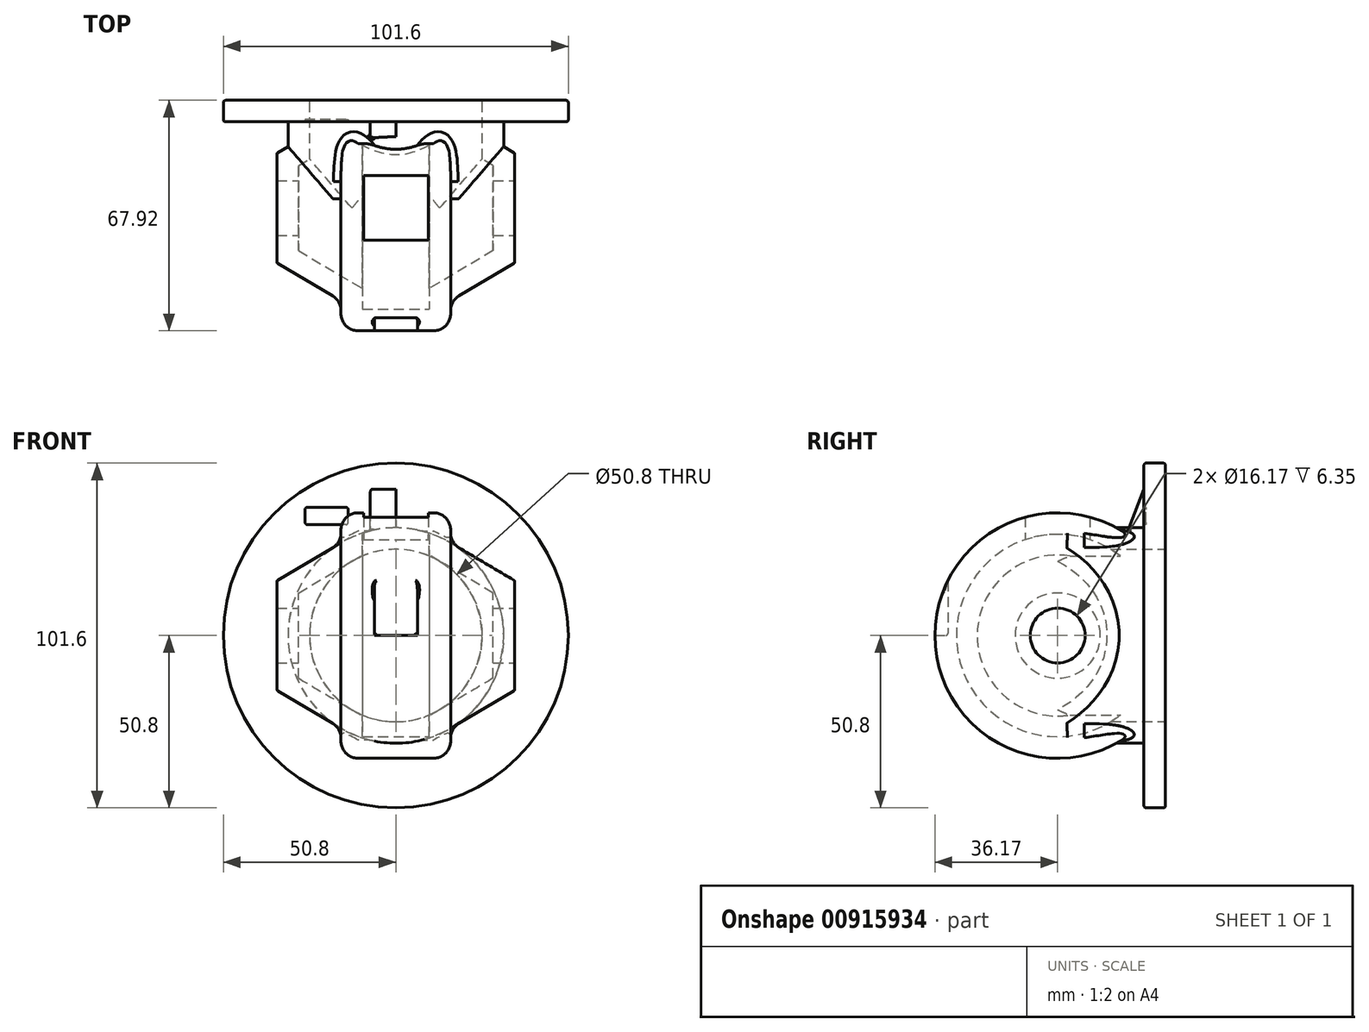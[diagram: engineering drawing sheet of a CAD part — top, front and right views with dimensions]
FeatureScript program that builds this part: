
annotation { "Feature Type Name" : "Feature", "Feature Type Description" : "" }
export const myFeature = defineFeature(function(context is Context, id is Id, definition is map)
    precondition{}
    {
        {
            var Q0;
            Q0=qCreatedBy(makeId("Front.planeOp"),FACE);
            var sketch = newSketch(context, id + "F0", { "sketchPlane" : qUnion([Q0])});
            skCircle(sketch, "E0", {"center": v(0, 0) * mm, "radius": 50.8 * mm});
            skSolve(sketch);
        }
        {
            var Q0;
            Q0=makeQuery(id+"F0.imprint","IMPRINT",FACE,{"disambiguationData":[TD([[makeQuery(id+"F0.imprint","IMPRINT",EDGE,{"derivedFrom":sQuery(id+"F0.wireOp",EDGE,"E0")}),1.0]])]});
            extrude(context, id + "F1", {"entities" : qUnion([Q0]), "depth" : 6.35 * mm, "offsetDistance" : 25.4 * mm});
        }
        {
            var Q0;
            Q0=makeQuery(id+"F1.opExtrude","CAP_FACE",FACE,{"disambiguationData":[OSD([sQuery(id+"F0.wireOp",EDGE,"E0")])],"isStart":false});
            var sketch = newSketch(context, id + "F2", { "sketchPlane" : qUnion([Q0])});
            skCircle(sketch, "E1", {"center": v(0, 0) * mm, "radius": 31.75 * mm});
            skCircle(sketch, "E2", {"center": v(0, 0) * mm, "radius": 25.4 * mm});
            skSolve(sketch);
        }
        {
            var Q0;
            Q0=makeQuery(id+"F2.imprint","IMPRINT",FACE,{"disambiguationData":[TD([[makeQuery(id+"F2.imprint","IMPRINT",EDGE,{"derivedFrom":sQuery(id+"F2.wireOp",EDGE,"E1")}),1.0]])]});
            extrude(context, id + "F3", {"entities" : qUnion([Q0]), "operationType" : NewBodyOperationType.ADD, "depth" : 25.4 * mm, "offsetDistance" : 25.4 * mm});
        }
        {
            var Q0;
            Q0=makeQuery(id+"F3.opExtrude","CAP_FACE",FACE,{"disambiguationData":[OSD([sQuery(id+"F2.wireOp",EDGE,"E1")])],"isStart":false});
            var sketch = newSketch(context, id + "F4", { "sketchPlane" : qUnion([Q0])});
            skLineSegment(sketch, "E3.top", {"start": v(16.16, 36.17) * mm, "end": v(-16.16, 36.17) * mm});
            skLineSegment(sketch, "E3.left", {"start": v(16.16, 27.33) * mm, "end": v(16.16, 36.17) * mm});
            skLineSegment(sketch, "E3.right", {"start": v(-16.16, 27.33) * mm, "end": v(-16.16, 36.17) * mm});
            skPoint(sketch, "E3.middle", {"position": v(0, 31.75) * mm});
            skLineSegment(sketch, "E4", {"start": v(-16.16, 27.33) * mm, "end": v(-35.03, 16.17) * mm});
            skLineSegment(sketch, "E5", {"start": v(-16.16, 27.33) * mm, "end": v(-16.16, -36.17) * mm, "construction": true});
            skLineSegment(sketch, "E6.MirrorCS", {"start": v(16.16, 27.33) * mm, "end": v(35.03, 16.17) * mm});
            skLineSegment(sketch, "E7.MirrorCS", {"start": v(16.16, 27.33) * mm, "end": v(16.16, -36.17) * mm, "construction": true});
            skLineSegment(sketch, "E8", {"start": v(-35.03, 16.17) * mm, "end": v(-35.03, 0) * mm, "construction": true});
            skLineSegment(sketch, "E9", {"start": v(35.03, 16.17) * mm, "end": v(35.03, 0) * mm, "construction": true});
            skLineSegment(sketch, "E10", {"start": v(35.03, 8.08) * mm, "end": v(35.03, 16.17) * mm});
            skLineSegment(sketch, "E11", {"start": v(-35.03, 16.17) * mm, "end": v(-35.03, 8.08) * mm});
            skLineSegment(sketch, "E12", {"start": v(-35.03, 0) * mm, "end": v(35.03, 0) * mm, "construction": true});
            skLineSegment(sketch, "E13.0", {"start": v(-28.68, 12.55) * mm, "end": v(-28.68, 8.08) * mm});
            skLineSegment(sketch, "E13.1", {"start": v(-9.81, 23.7) * mm, "end": v(-28.68, 12.55) * mm});
            skLineSegment(sketch, "E13.2", {"start": v(-9.81, 23.7) * mm, "end": v(-9.81, 29.82) * mm});
            skLineSegment(sketch, "E13.3", {"start": v(28.68, 12.55) * mm, "end": v(28.68, 8.08) * mm});
            skLineSegment(sketch, "E13.4", {"start": v(9.81, 23.7) * mm, "end": v(28.68, 12.55) * mm});
            skLineSegment(sketch, "E13.5", {"start": v(9.81, 23.7) * mm, "end": v(9.81, 29.82) * mm});
            skLineSegment(sketch, "E13.6", {"start": v(9.81, 29.82) * mm, "end": v(-9.81, 29.82) * mm});
            skLineSegment(sketch, "E14", {"start": v(-35.03, 8.08) * mm, "end": v(35.03, 8.08) * mm, "construction": true});
            skLineSegment(sketch, "E15", {"start": v(-35.03, 8.08) * mm, "end": v(-28.68, 8.08) * mm});
            skLineSegment(sketch, "E16", {"start": v(28.68, 8.08) * mm, "end": v(35.03, 8.08) * mm});
            skLineSegment(sketch, "E17", {"start": v(-35.03, 8.08) * mm, "end": v(-35.03, 0) * mm});
            skLineSegment(sketch, "E18", {"start": v(35.03, 0) * mm, "end": v(35.03, 8.08) * mm});
            skLineSegment(sketch, "E19", {"start": v(-35.03, 0) * mm, "end": v(35.03, 0) * mm});
            skSolve(sketch);
        }
        {
            var Q0;
            Q0 = qSketchRegion(id + "F4", true);
            var Q1;
            Q1=sQuery(id+"F4.wireOp",EDGE,"E12");
            revolve(context, id + "F5", {"operationType" : NewBodyOperationType.ADD, "surfaceOperationType" : NewSurfaceOperationType.NEW, "entities" : qUnion([Q0]), "axis" : qUnion([Q1]), "revolveType" : RevolveType.FULL});
        }
        {
            var Q0;
            Q0=qCreatedBy(makeId("Right.planeOp"),FACE);
            cPlane(context, id + "F6", {"entities" : qUnion([Q0]), "cplaneType" : CPlaneType.OFFSET, "offset" : 7.62 * mm, "oppositeDirection" : true, "width" : 152.4 * mm, "height" : 152.4 * mm});
        }
        {
            var Q0;
            Q0=qCreatedBy(id+"F6.planeOp",FACE);
            var sketch = newSketch(context, id + "F7", { "sketchPlane" : qUnion([Q0])});
            skLineSegment(sketch, "E20", {"start": v(-6.35, 29.8) * mm, "end": v(-11.51, 29.8) * mm});
            skLineSegment(sketch, "E21", {"start": v(-11.51, 29.8) * mm, "end": v(-6.35, 43.09) * mm});
            skLineSegment(sketch, "E22", {"start": v(-6.35, 43.09) * mm, "end": v(-6.35, 29.8) * mm});
            skSolve(sketch);
        }
        {
            var Q0;
            Q0=makeQuery(id+"F7.imprint","IMPRINT",FACE,{"disambiguationData":[TD([[makeQuery(id+"F7.imprint","IMPRINT",EDGE,{"derivedFrom":sQuery(id+"F7.wireOp",EDGE,"E20")}),-1.0]])]});
            var Q1;
            Q1=qCreatedBy(makeId("Right.planeOp"),FACE);
            extrude(context, id + "F8", {"entities" : qUnion([Q0]), "operationType" : NewBodyOperationType.ADD, "endBound" : BoundingType.UP_TO_SURFACE, "depth" : 2.03 * mm, "endBoundEntityFace" : qUnion([Q1]), "offsetDistance" : 25.4 * mm});
        }
        {
            var Q0;
            Q0=qCreatedBy(makeId("Top.planeOp"),FACE);
            var sketch = newSketch(context, id + "F9", { "sketchPlane" : qUnion([Q0])});
            skPoint(sketch, "E23.0", {"position": v(-16.16, -31.75) * mm});
            skPoint(sketch, "E24.0", {"position": v(16.16, -31.75) * mm});
            skLineSegment(sketch, "E25", {"start": v(16.16, -31.75) * mm, "end": v(-16.16, -31.75) * mm, "construction": true});
            skLineSegment(sketch, "E26.bottom", {"start": v(-9.52, -41.27) * mm, "end": v(9.53, -41.27) * mm});
            skLineSegment(sketch, "E26.top", {"start": v(-9.52, -22.23) * mm, "end": v(9.52, -22.23) * mm});
            skLineSegment(sketch, "E26.left", {"start": v(-9.52, -41.27) * mm, "end": v(-9.52, -22.23) * mm});
            skLineSegment(sketch, "E26.right", {"start": v(9.53, -41.27) * mm, "end": v(9.52, -22.23) * mm});
            skPoint(sketch, "E26.middle", {"position": v(0, -31.75) * mm});
            skSolve(sketch);
        }
        {
            var Q0;
            Q0=makeQuery(id+"F9.imprint","IMPRINT",FACE,{"disambiguationData":[TD([[makeQuery(id+"F9.imprint","IMPRINT",EDGE,{"derivedFrom":sQuery(id+"F9.wireOp",EDGE,"E26.bottom")}),1.0]])]});
            extrude(context, id + "F10", {"entities" : qUnion([Q0]), "operationType" : NewBodyOperationType.REMOVE, "endBound" : BoundingType.THROUGH_ALL, "depth" : 93.73 * mm, "offsetDistance" : 25.4 * mm});
        }
        {
            var Q0;
            Q0=qCreatedBy(makeId("Top.planeOp"),FACE);
            var sketch = newSketch(context, id + "F11", { "sketchPlane" : qUnion([Q0])});
            skLineSegment(sketch, "E27", {"start": v(8.66, -67.92) * mm, "end": v(-8.66, -67.92) * mm, "construction": true});
            skLineSegment(sketch, "E28.bottom", {"start": v(6.35, -67.92) * mm, "end": v(-6.35, -67.92) * mm});
            skLineSegment(sketch, "E28.top", {"start": v(6.35, -64.11) * mm, "end": v(-6.35, -64.11) * mm});
            skLineSegment(sketch, "E28.left", {"start": v(6.35, -67.92) * mm, "end": v(6.35, -64.11) * mm});
            skLineSegment(sketch, "E28.right", {"start": v(-6.35, -67.92) * mm, "end": v(-6.35, -64.11) * mm});
            skPoint(sketch, "E28.middle", {"position": v(0, -66.02) * mm});
            skPoint(sketch, "E28.middle.positionSnap0", {"position": v(0, -67.92) * mm});
            skPoint(sketch, "E28.centerSnap0", {"position": v(0, -67.92) * mm});
            skSolve(sketch);
        }
        {
            var Q0;
            Q0 = qSketchRegion(id + "F11", true);
            extrude(context, id + "F12", {"entities" : qUnion([Q0]), "operationType" : NewBodyOperationType.REMOVE, "endBound" : BoundingType.THROUGH_ALL, "depth" : 51.3 * mm, "offsetDistance" : 25.4 * mm});
        }
        {
            var Q0;
            Q0=makeQuery(id+"F1.opExtrude","CAP_FACE",FACE,{"disambiguationData":[OSD([sQuery(id+"F0.wireOp",EDGE,"E0")])],"isStart":false});
            var sketch = newSketch(context, id + "F13", { "sketchPlane" : qUnion([Q0])});
            skLineSegment(sketch, "E29.bottom", {"start": v(-14.02, 32.7) * mm, "end": v(-26.72, 32.7) * mm});
            skLineSegment(sketch, "E29.top", {"start": v(-14.02, 37.77) * mm, "end": v(-26.72, 37.77) * mm});
            skLineSegment(sketch, "E29.left", {"start": v(-14.02, 32.7) * mm, "end": v(-14.02, 37.77) * mm});
            skLineSegment(sketch, "E29.right", {"start": v(-26.72, 32.7) * mm, "end": v(-26.72, 37.77) * mm});
            skPoint(sketch, "E29.middle", {"position": v(-20.37, 35.23) * mm});
            skSolve(sketch);
        }
        {
            var Q0;
            Q0=makeQuery(id+"F13.imprint","IMPRINT",FACE,{"disambiguationData":[TD([[makeQuery(id+"F13.imprint","IMPRINT",EDGE,{"derivedFrom":sQuery(id+"F13.wireOp",EDGE,"E29.bottom")}),-1.0]])]});
            extrude(context, id + "F14", {"entities" : qUnion([Q0]), "operationType" : NewBodyOperationType.REMOVE, "oppositeDirection" : true, "depth" : 0.64 * mm, "offsetDistance" : 25.4 * mm});
        }
        {
            var Q0;
            {var subQ0=sQuery(id+"F4.wireOp",EDGE,"E17");Q0=makeQuery(id+"F4.imprint","IMPRINT",FACE,{"disambiguationData":[TD([[makeQuery(id+"F4.imprint","IMPRINT",EDGE,{"derivedFrom":subQ0}),1.0]])]});}
            var Q1;
            {var subQ7=sQuery(id+"F4.wireOp",EDGE,"E13.0");Q1=makeQuery(id+"F4.imprint","IMPRINT",FACE,{"disambiguationData":[TD([[makeQuery(id+"F4.imprint","IMPRINT",EDGE,{"derivedFrom":subQ7}),1.0]])]});}
            var Q2;
            {var subQ0=sQuery(id+"F4.wireOp",EDGE,"E19");var subQ1=makeQuery(id+"F3.opExtrude","CAP_EDGE",EDGE,{"disambiguationData":[OSD([sQuery(id+"F2.wireOp",EDGE,"E2")])],"isStart":false});var subQ2=makeQuery(id+"F4.imprint","INTERSECT",VERTEX,{"disambiguationData":[OD(0.0)],"derivedFrom":[subQ1,subQ0]});Q2=makeQuery(id+"F4.imprint","IMPRINT",FACE,{"disambiguationData":[TD([[makeQuery(id+"F4.imprint","IMPRINT",EDGE,{"disambiguationData":[TD([[subQ2,-1.0]])],"derivedFrom":subQ0}),1.0]])]});}
            var Q3;
            {var subQ4=sQuery(id+"F4.wireOp",EDGE,"E13.2");Q3=makeQuery(id+"F4.imprint","IMPRINT",FACE,{"disambiguationData":[TD([[makeQuery(id+"F4.imprint","IMPRINT",EDGE,{"derivedFrom":subQ4}),-1.0]])]});}
            var Q4;
            {var subQ6=sQuery(id+"F4.wireOp",EDGE,"E13.3");Q4=makeQuery(id+"F4.imprint","IMPRINT",FACE,{"disambiguationData":[TD([[makeQuery(id+"F4.imprint","IMPRINT",EDGE,{"derivedFrom":subQ6}),-1.0]])]});}
            var Q5;
            {var subQ0=sQuery(id+"F4.wireOp",EDGE,"E18");Q5=makeQuery(id+"F4.imprint","IMPRINT",FACE,{"disambiguationData":[TD([[makeQuery(id+"F4.imprint","IMPRINT",EDGE,{"derivedFrom":subQ0}),1.0]])]});}
            var Q6;
            Q6=sQuery(id+"F4.wireOp",EDGE,"E19");
            revolve(context, id + "F15", {"operationType" : NewBodyOperationType.REMOVE, "surfaceOperationType" : NewSurfaceOperationType.NEW, "entities" : qUnion([Q0, Q1, Q2, Q3, Q4, Q5]), "axis" : qUnion([Q6]), "revolveType" : RevolveType.FULL, "oppositeDirection" : true});
        }
        {
            var Q0;
            Q0=makeQuery(id+"F3.boolean.opBoolean","SPLIT",FACE,{"disambiguationData":[TD([makeQuery(id+"F3.opExtrude","SWEPT_FACE",FACE,{"disambiguationData":[OSD([sQuery(id+"F2.wireOp",EDGE,"E2")])]})])],"derivedFrom":makeQuery(id+"F1.opExtrude","CAP_FACE",FACE,{"disambiguationData":[OSD([sQuery(id+"F0.wireOp",EDGE,"E0")])],"isStart":false})});
            var sketch = newSketch(context, id + "F16", { "sketchPlane" : qUnion([Q0])});
            skCircle(sketch, "E30.0", {"center": v(0, 0) * mm, "radius": 25.4 * mm});
            skSolve(sketch);
        }
        {
            var Q0;
            Q0 = qSketchRegion(id + "F16", true);
            extrude(context, id + "F17", {"entities" : qUnion([Q0]), "operationType" : NewBodyOperationType.REMOVE, "endBound" : BoundingType.THROUGH_ALL, "oppositeDirection" : true, "depth" : 25.4 * mm, "offsetDistance" : 25.4 * mm});
        }
        {
            var Q0;
            Q0=makeQuery(id+"F1.opExtrude","CAP_FACE",FACE,{"disambiguationData":[OSD([sQuery(id+"F0.wireOp",EDGE,"E0")])],"isStart":true});
            var sketch = newSketch(context, id + "F18", { "sketchPlane" : qUnion([Q0])});
            skCircle(sketch, "E31.0", {"center": v(0, 0) * mm, "radius": 25.4 * mm});
            skSolve(sketch);
        }
        {
            var Q0;
            Q0 = qSketchRegion(id + "F18", true);
            var Q1;
            Q1=makeQuery(id+"F5.boolean.opBoolean","INTERSECT",VERTEX,{"disambiguationData":[OD(1.0)],"derivedFrom":[makeQuery(id+"F3.opExtrude","SWEPT_FACE",FACE,{"disambiguationData":[OSD([sQuery(id+"F2.wireOp",EDGE,"E1")])]}),makeQuery(id+"F5.opRevolve","SWEPT_FACE",FACE,{"disambiguationData":[OSD([sQuery(id+"F4.wireOp",EDGE,"E3.right")])]}),makeQuery(id+"F5.opRevolve","SWEPT_FACE",FACE,{"disambiguationData":[OSD([sQuery(id+"F4.wireOp",EDGE,"E4")])]})]});
            extrude(context, id + "F19", {"entities" : qUnion([Q0]), "operationType" : NewBodyOperationType.REMOVE, "endBound" : BoundingType.UP_TO_VERTEX, "oppositeDirection" : true, "depth" : 12.45 * mm, "endBoundEntityVertex" : qUnion([Q1]), "offsetDistance" : 25.4 * mm});
        }
        {
            var Q0;
            {var subQ0=sQuery(id+"F4.wireOp",EDGE,"E3.top");var subQ1=sQuery(id+"F4.wireOp",EDGE,"E3.right");Q0=makeQuery(id+"F5.boolean.opBoolean","SPLIT",EDGE,{"disambiguationData":[TD([makeQuery(id+"F3.opExtrude","SWEPT_FACE",FACE,{"disambiguationData":[OSD([sQuery(id+"F2.wireOp",EDGE,"E1")])]})])],"derivedFrom":makeQuery(id+"F5.opRevolve","SWEPT_EDGE",EDGE,{"disambiguationData":[OSD([subQ0,subQ1])]})});}
            var Q1;
            {var subQ0=sQuery(id+"F4.wireOp",EDGE,"E3.left");var subQ1=sQuery(id+"F4.wireOp",EDGE,"E3.top");Q1=makeQuery(id+"F5.boolean.opBoolean","SPLIT",EDGE,{"disambiguationData":[TD([makeQuery(id+"F3.opExtrude","SWEPT_FACE",FACE,{"disambiguationData":[OSD([sQuery(id+"F2.wireOp",EDGE,"E1")])]})])],"derivedFrom":makeQuery(id+"F5.opRevolve","SWEPT_EDGE",EDGE,{"disambiguationData":[OSD([subQ1,subQ0])]})});}
            var Q2;
            {var subQ0=sQuery(id+"F2.wireOp",EDGE,"E1");var subQ1=sQuery(id+"F4.wireOp",EDGE,"E3.right");var subQ2=sQuery(id+"F4.wireOp",EDGE,"E4");Q2=makeQuery(id+"F5.boolean.opBoolean","SPLIT",EDGE,{"disambiguationData":[TD([makeQuery(id+"F3.opExtrude","SWEPT_FACE",FACE,{"disambiguationData":[OSD([subQ0])]}),makeQuery(id+"F5.opRevolve","SWEPT_FACE",FACE,{"disambiguationData":[OSD([subQ1])]}),makeQuery(id+"F5.opRevolve","SWEPT_FACE",FACE,{"disambiguationData":[OSD([subQ2])]})])],"derivedFrom":makeQuery(id+"F5.opRevolve","SWEPT_EDGE",EDGE,{"disambiguationData":[OSD([subQ0,subQ1,subQ2])]})});}
            var Q3;
            {var subQ0=sQuery(id+"F2.wireOp",EDGE,"E1");var subQ1=sQuery(id+"F4.wireOp",EDGE,"E3.left");var subQ2=sQuery(id+"F4.wireOp",EDGE,"E6.MirrorCS");Q3=makeQuery(id+"F5.boolean.opBoolean","SPLIT",EDGE,{"disambiguationData":[TD([makeQuery(id+"F3.opExtrude","SWEPT_FACE",FACE,{"disambiguationData":[OSD([subQ0])]}),makeQuery(id+"F5.opRevolve","SWEPT_FACE",FACE,{"disambiguationData":[OSD([subQ1])]}),makeQuery(id+"F5.opRevolve","SWEPT_FACE",FACE,{"disambiguationData":[OSD([subQ2])]})])],"derivedFrom":makeQuery(id+"F5.opRevolve","SWEPT_EDGE",EDGE,{"disambiguationData":[OSD([subQ0,subQ1,subQ2])]})});}
            fillet(context, id + "F20", {"entities" : qUnion([Q0, Q1, Q2, Q3]), "radius" : 5.08 * mm, "tangentPropagation" : true, "allowEdgeOverflow" : false});
        }
        {
            var Q0;
            Q0=makeQuery(id+"F1.opExtrude","CAP_EDGE",EDGE,{"disambiguationData":[OSD([sQuery(id+"F0.wireOp",EDGE,"E0")])],"isStart":false});
            var Q1;
            Q1=makeQuery(id+"F14.boolean.opBoolean","COPY",EDGE,{"derivedFrom":makeQuery(id+"F14.opExtrude","SWEPT_EDGE",EDGE,{"disambiguationData":[OSD([sQuery(id+"F13.wireOp",EDGE,"E29.bottom"),sQuery(id+"F13.wireOp",EDGE,"E29.left")])]})});
            var Q2;
            Q2=makeQuery(id+"F14.boolean.opBoolean","COPY",EDGE,{"derivedFrom":makeQuery(id+"F14.opExtrude","SWEPT_EDGE",EDGE,{"disambiguationData":[OSD([sQuery(id+"F13.wireOp",EDGE,"E29.top"),sQuery(id+"F13.wireOp",EDGE,"E29.left")])]})});
            var Q3;
            Q3=makeQuery(id+"F14.boolean.opBoolean","COPY",EDGE,{"derivedFrom":makeQuery(id+"F14.opExtrude","SWEPT_EDGE",EDGE,{"disambiguationData":[OSD([sQuery(id+"F13.wireOp",EDGE,"E29.bottom"),sQuery(id+"F13.wireOp",EDGE,"E29.right")])]})});
            var Q4;
            Q4=makeQuery(id+"F14.boolean.opBoolean","COPY",EDGE,{"derivedFrom":makeQuery(id+"F14.opExtrude","SWEPT_EDGE",EDGE,{"disambiguationData":[OSD([sQuery(id+"F13.wireOp",EDGE,"E29.top"),sQuery(id+"F13.wireOp",EDGE,"E29.right")])]})});
            var Q5;
            Q5=makeQuery(id+"F6ZTliT6EXj1Yaa_1.1.F14.boolean.opBoolean","COPY",EDGE,{"derivedFrom":makeQuery(id+"F6ZTliT6EXj1Yaa_1.1.F14.opExtrude","SWEPT_EDGE",EDGE,{"disambiguationData":[OSD([sQuery(id+"F13.wireOp",EDGE,"E29.bottom"),sQuery(id+"F13.wireOp",EDGE,"E29.right")])]})});
            var Q6;
            Q6=makeQuery(id+"F6ZTliT6EXj1Yaa_1.1.F14.boolean.opBoolean","COPY",EDGE,{"derivedFrom":makeQuery(id+"F6ZTliT6EXj1Yaa_1.1.F14.opExtrude","SWEPT_EDGE",EDGE,{"disambiguationData":[OSD([sQuery(id+"F13.wireOp",EDGE,"E29.bottom"),sQuery(id+"F13.wireOp",EDGE,"E29.left")])]})});
            var Q7;
            Q7=makeQuery(id+"F6ZTliT6EXj1Yaa_1.1.F14.boolean.opBoolean","COPY",EDGE,{"derivedFrom":makeQuery(id+"F6ZTliT6EXj1Yaa_1.1.F14.opExtrude","SWEPT_EDGE",EDGE,{"disambiguationData":[OSD([sQuery(id+"F13.wireOp",EDGE,"E29.top"),sQuery(id+"F13.wireOp",EDGE,"E29.left")])]})});
            var Q8;
            Q8=makeQuery(id+"F6ZTliT6EXj1Yaa_1.1.F14.boolean.opBoolean","COPY",EDGE,{"derivedFrom":makeQuery(id+"F6ZTliT6EXj1Yaa_1.1.F14.opExtrude","SWEPT_EDGE",EDGE,{"disambiguationData":[OSD([sQuery(id+"F13.wireOp",EDGE,"E29.top"),sQuery(id+"F13.wireOp",EDGE,"E29.right")])]})});
            var Q9;
            Q9=makeQuery(id+"F3.opExtrude","CAP_EDGE",EDGE,{"disambiguationData":[OSD([sQuery(id+"F2.wireOp",EDGE,"E1")])],"isStart":true});
            var Q10;
            Q10=makeQuery(id+"F8.opExtrude","CAP_EDGE",EDGE,{"disambiguationData":[OSD([sQuery(id+"F7.wireOp",EDGE,"E22")])],"isStart":true});
            var Q11;
            Q11=makeQuery(id+"F8.boolean.opBoolean","INTERSECT",EDGE,{"derivedFrom":[makeQuery(id+"F3.opExtrude","SWEPT_FACE",FACE,{"disambiguationData":[OSD([sQuery(id+"F2.wireOp",EDGE,"E1")])]}),makeQuery(id+"F8.opExtrude","CAP_FACE",FACE,{"disambiguationData":[OSD([sQuery(id+"F7.wireOp",EDGE,"E20"),sQuery(id+"F7.wireOp",EDGE,"E21"),sQuery(id+"F7.wireOp",EDGE,"E22")])],"isStart":true})]});
            var Q12;
            Q12=makeQuery(id+"F8.opExtrude","CAP_EDGE",EDGE,{"disambiguationData":[OSD([sQuery(id+"F7.wireOp",EDGE,"E21")])],"isStart":true});
            var Q13;
            Q13=makeQuery(id+"FyizzrJlf40D4wo_1.1.F8.opExtrude","CAP_EDGE",EDGE,{"disambiguationData":[OSD([sQuery(id+"F7.wireOp",EDGE,"E21")])],"isStart":true});
            var Q14;
            Q14=makeQuery(id+"FyizzrJlf40D4wo_1.1.F8.opExtrude","CAP_EDGE",EDGE,{"disambiguationData":[OSD([sQuery(id+"F7.wireOp",EDGE,"E22")])],"isStart":true});
            var Q15;
            Q15=makeQuery(id+"F5.opRevolve","SWEPT_EDGE",EDGE,{"disambiguationData":[OSD([sQuery(id+"F4.wireOp",EDGE,"E4"),sQuery(id+"F4.wireOp",EDGE,"E11")])]});
            var Q16;
            Q16=makeQuery(id+"F5.opRevolve","SWEPT_EDGE",EDGE,{"disambiguationData":[OSD([sQuery(id+"F4.wireOp",EDGE,"E6.MirrorCS"),sQuery(id+"F4.wireOp",EDGE,"E10")])]});
            var Q17;
            {var subQ0=sQuery(id+"F11.wireOp",EDGE,"E28.top");Q17=makeQuery(id+"F5MhUiyj64DYXYs_1.1.F12.boolean.opBoolean","MERGE",FACE,{"derivedFrom":[makeQuery(id+"F12.boolean.opBoolean","COPY",FACE,{"derivedFrom":makeQuery(id+"F12.opExtrude","SWEPT_FACE",FACE,{"disambiguationData":[OSD([subQ0])]})})],"fromTools":[makeQuery(id+"F5MhUiyj64DYXYs_1.1.F12.opExtrude","SWEPT_FACE",FACE,{"disambiguationData":[OSD([subQ0])]})]});}
            var Q18;
            Q18=makeQuery(id+"F1.opExtrude","CAP_EDGE",EDGE,{"disambiguationData":[OSD([sQuery(id+"F0.wireOp",EDGE,"E0")])],"isStart":true});
            fillet(context, id + "F21", {"entities" : qUnion([Q0, Q1, Q2, Q3, Q4, Q5, Q6, Q7, Q8, Q9, Q10, Q11, Q12, Q13, Q14, Q15, Q16, Q17, Q18]), "radius" : 0.64 * mm, "tangentPropagation" : true, "allowEdgeOverflow" : false});
        }
    });
